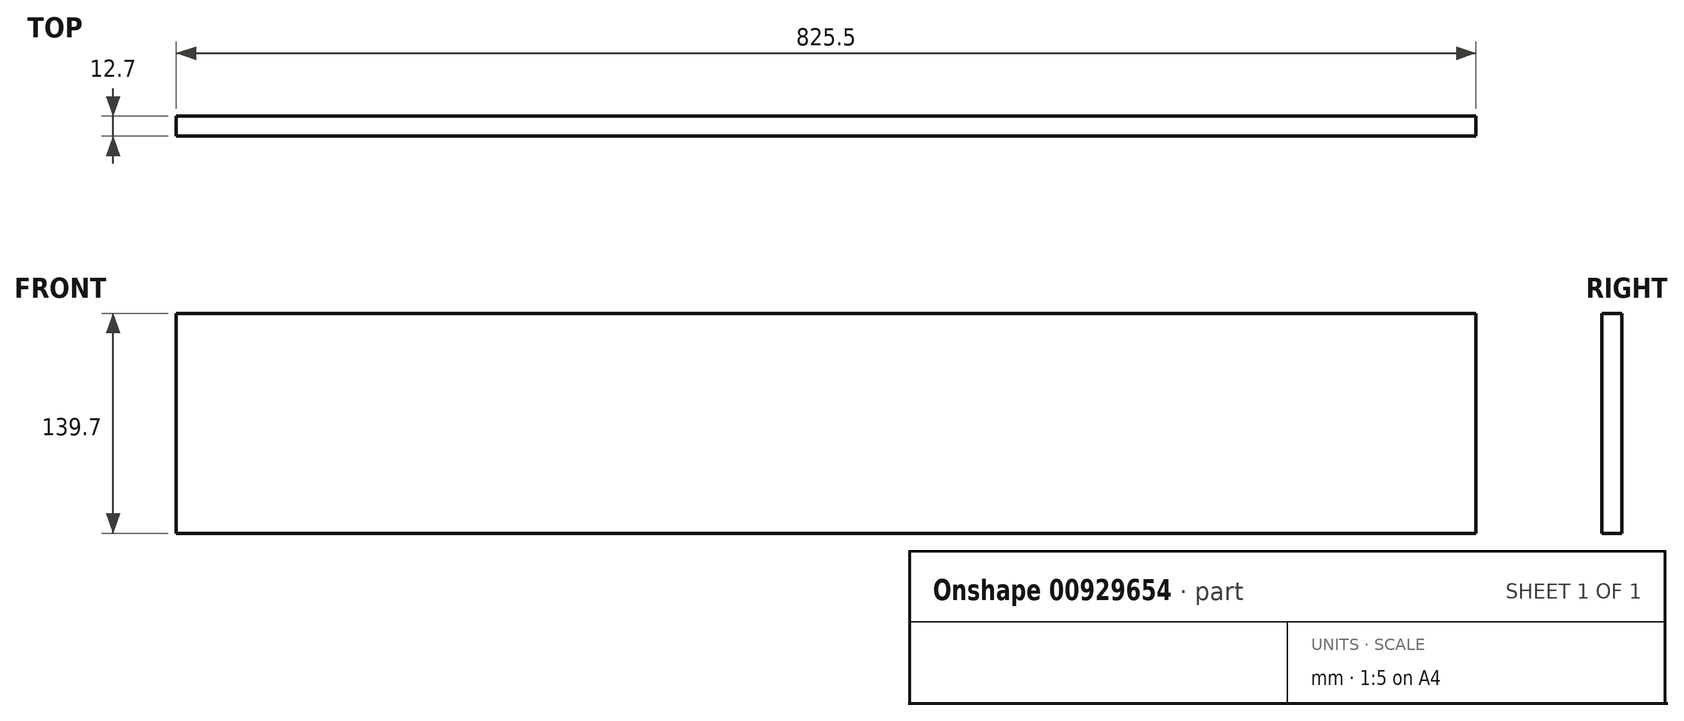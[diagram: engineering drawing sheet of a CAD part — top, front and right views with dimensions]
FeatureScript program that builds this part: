
annotation { "Feature Type Name" : "Feature", "Feature Type Description" : "" }
export const myFeature = defineFeature(function(context is Context, id is Id, definition is map)
    precondition{}
    {
        {
            var Q0;
            Q0=qCreatedBy(makeId("Front.planeOp"),FACE);
            var sketch = newSketch(context, id + "F0", { "sketchPlane" : qUnion([Q0])});
            skLineSegment(sketch, "E0.bottom", {"start": v(412.75, 69.85) * mm, "end": v(-412.75, 69.85) * mm});
            skLineSegment(sketch, "E0.top", {"start": v(412.75, -69.85) * mm, "end": v(-412.75, -69.85) * mm});
            skLineSegment(sketch, "E0.left", {"start": v(412.75, 69.85) * mm, "end": v(412.75, -69.85) * mm});
            skLineSegment(sketch, "E0.right", {"start": v(-412.75, 69.85) * mm, "end": v(-412.75, -69.85) * mm});
            skPoint(sketch, "E0.middle", {"position": v(0, 0) * mm});
            skSolve(sketch);
        }
        {
            var Q0;
            Q0 = qSketchRegion(id + "F0", true);
            extrude(context, id + "F1", {"entities" : qUnion([Q0]), "depth" : 12.7 * mm, "offsetDistance" : 25.4 * mm});
        }
    });
